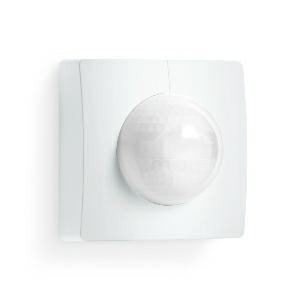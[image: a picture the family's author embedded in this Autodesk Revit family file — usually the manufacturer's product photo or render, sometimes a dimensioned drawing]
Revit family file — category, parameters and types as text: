
# Revit family: is_3180_010553
name_source: partatom
category: Elektroinstallationen
revit_build: Autodesk Revit 2016 (Build: 20190508_0715(x64)
units: mm (PartAtom-declared; Revit-internal decimal feet)

## family parameters
Basisbauteil = Fläche
Beim Laden mit Abzugskörper schneiden = Nein
Bemaßung runder Anschluss = Durchmesser verwenden
Beschriftungsausrichtung beibehalten = Nein
Gemeinsam genutzt = Nein
Raumberechnungspunkt = Nein
Teiletyp = Normal

## types (1)
- IS 3180
    Apparent Load = 0 VA
    Beschreibung = Type: Motion detectors; Dimensions (L x W x H): 65 x 95 x 95 mm; Mains power supply: 220 – 240 V / 50 – 60 Hz; Sensor Technology: passive infrared; Application, place: Outdoors, Indoors; Application, room: corridor / aisle, function room / ancillary room, stairwell, multi-storey / underground car park, outdoors, all round the building, courtyard & driveway, Indoors; Installation site: wall, corner; Installation: Surface wiring; Switching zones: 448 switching zones; Electronic scalability: No; Mechanical scalability: No; Mounting height: 1,80 – 2,50 m; Optimum mounting height: 2 m; Detection angle: 180 °; Angle of aperture: 90 °; Sneak-by guard: Yes; Capability of masking out individual segments: Yes; Reach, radial: r = 3 m (14 m²) / r = 4 m (25 m²); Reach, tangential: r = 6 m (57 m²) / r = 20 m (628 m²); Twilight setting TEACH: Yes; Twilight setting: 2 – 1000 lx; Time setting: 5 sec – 15 min; Control output, Dali: Broadcast 1x30 electronic ballasts; Constant-lighting control: Yes; Basic light level function: Yes; Basic light level function in per cent: 10 – 50 %; Basic light level function time: 1-30 min, all night; Basic light level function percentage, from: 10 %; Basic light level function percentage, up to: 50 %; Functions: Normal / test mode, Manual ON / ON-OFF, Constant-lighting control ON-OFF; Settings via: Remote control, Potentiometers, Smart Remote; With remote control: No; Interconnection: Yes; IP-rating: IP54; Material: Plastic; Ambient temperature: -20 – 50 °C; Colour: white; Colour, RAL: 9003; Manufacturer's Warranty: 5 years; Version: DALI-2 Application Controller - surface, sq.; PU1, EAN: 4007841010553
    Height = 95 mm
    Hersteller = Steinel
    Length = 65 mm
    Maximum range = 22.153 m
    ModVariant = Nein
    Modell = 010553
    Mounting Type = Surface mounted
    Number of Poles = 1
    OnlyDefault = Ja
    Power Factor = 1
    Product Name = IS 3180
    Product group = Sensor-switched indoor light
    ProductGroupID = 30
    Protection Class = Protection class
    Protection Degree = IP 54
    RlxData = <blob elided: 167405 chars, md5=ddc9b40e>
    Sensor characteristics = Semi circular 145°-300°
    Sensor type = Passive (infrared)
    SensorDataFile = <blob elided: 5082 chars, md5=d953030a>
    Type of entry = Motion
    Typenbild = produkt1_010553.jpg
    Typenkommentare = Product without accessories
    URL = http://relux.com
    VarID = ---
    Voltage = 0 V
    Vorgabe-Ansicht = 1800 mm
    Weight = 0.00 kg
    Width = 95 mm

## geometry (parser evidence)
native form markers: Sweep x13
no freeform markers — native parametric forms only
